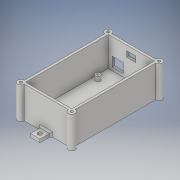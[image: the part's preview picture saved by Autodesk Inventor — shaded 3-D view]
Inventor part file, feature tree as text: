
AUTODESK INVENTOR PART (.ipt)
format: ipt  version: 2019 (Build 230136000, 136)  size: 252,416 bytes
history: native  units: mm
features: extrude x9, sketch x9, projected_geometry x4, mirror x3, chamfer x2
ambient origin geometry x8: Origin, YZ Plane, XZ Plane, XY Plane, X Axis, Y Axis, Z Axis, Center Point
bodies: Solid1 (feature_tree)
feature tree (27):
  extrude  "Extrusion1"  Depth=110.0mm
  extrude  "Extrusion2"  Depth=3.0mm
  extrude  "Extrusion3"  Depth=3.0mm
  extrude  "Extrusion4"  Depth=37.0mm TaperAngle=0.0deg
  extrude  "Extrusion5"  Depth=92.0mm
  extrude  "Extrusion6"  Depth=2.5mm
  extrude  "Extrusion7"  Depth=2.5mm
  mirror  "Mirror1"
  mirror  "Mirror2"
  extrude  "Extrusion9"  Depth=5.92mm
  chamfer  "Chamfer1"  Distance=6.0mm
  extrude  "Extrusion10"  Depth=6.0mm
  mirror  "Mirror3"
  chamfer  "Chamfer2"  Distance=6.0mm
  sketch  "Sketch1"  dims[d0=64.0mm d1=110.0mm]
  sketch  "Sketch2"  dims[d2=3.0mm d3=0.0mm d4=3.0mm]
  projected_geometry  "Projected Loop1"
  sketch  "Sketch3"  dims[d5=3.0mm d6=3.0mm]
  sketch  "Sketch4"  dims[d7=3.0mm d8=37.0mm d9=0.0mm]
  sketch  "Sketch5"  dims[d15=46.16mm d16=92.0mm]
  projected_geometry  "Projected Loop2"
  sketch  "Sketch7"  dims[d17=2.5mm d18=2.5mm]
  projected_geometry  "Projected Loop3"
  sketch  "Sketch8"  dims[d19=2.5mm d20=2.5mm]
  sketch  "Sketch10"  dims[d21=79.0mm d22=5.92mm]
  sketch  "Sketch11"  dims[d23=5.92mm d24=6.0mm d25=6.0mm d26=6.0mm d27=6.0mm d28=6.0mm d29=6.0mm d30=6.0mm d31=0.0mm d33=2.0mm d34=12.0mm d35=14.0mm d36=6.0mm d37=0.0mm d38=18.0mm d39=7.0mm d40=11.5mm d41=23.25mm d42=23.25mm d43=6.0mm d44=0.0mm d45=40.0mm d46=0.0mm d47=3.3mm d48=20.0mm d49=0.0mm d56=4.0mm d57=12.0mm d58=21.757359mm d59=21.757359mm d60=14.0mm d61=0.0mm d62=2.0mm d63=2.0mm d64=45.0deg d65=5.2mm d66=6.0mm d67=6.0mm d68=12.0mm d69=0.0mm d70=2.0mm d71=2.0mm d72=45.0deg d73=5.0mm]
  projected_geometry  "Projected Loop4"
